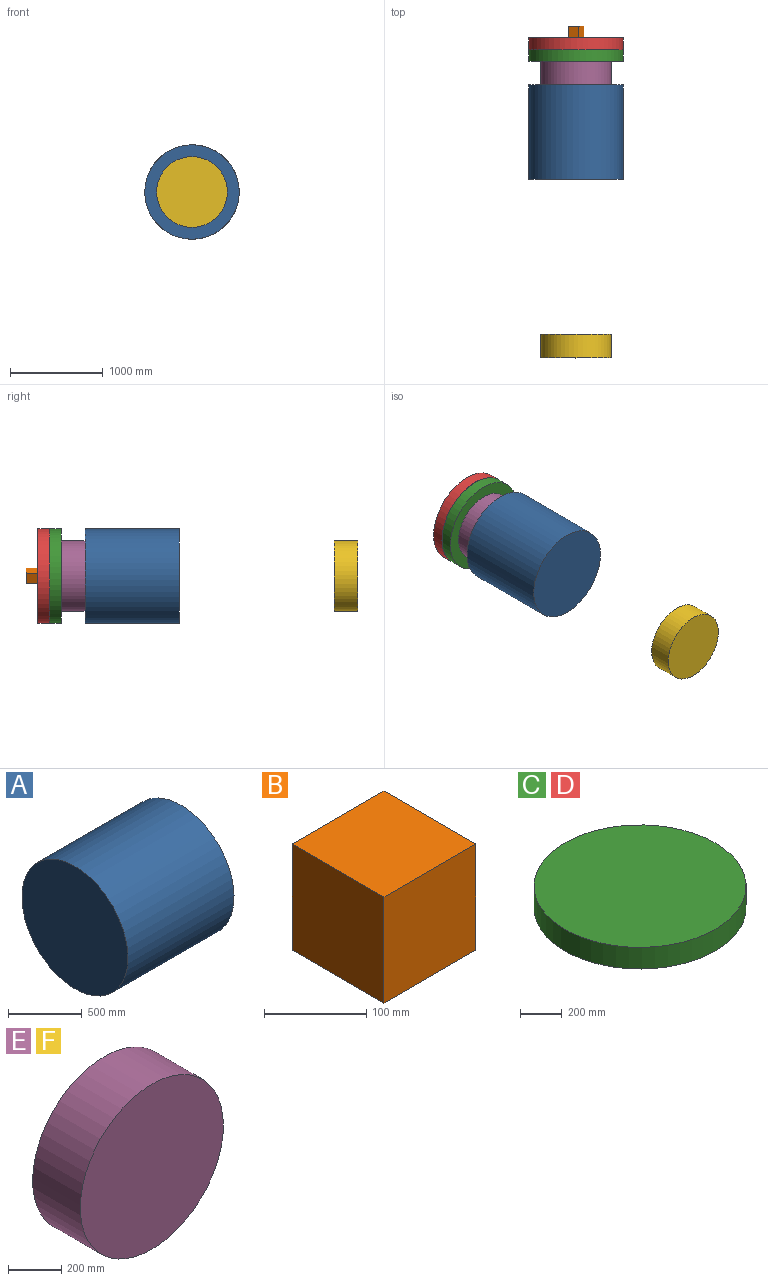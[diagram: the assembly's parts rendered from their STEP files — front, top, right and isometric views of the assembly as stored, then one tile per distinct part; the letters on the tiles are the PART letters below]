
ASSEMBLY  parts=6 mates=5
PART A: 3 faces, bbox 1016x1016x1016 mm
  f0: cylinder r=508mm len=1016mm, axis (-1,0,0), area 3242927.9mm2, adj f1,f2
  f1: plane 1016x1016mm, normal (1,0,0), area 810732mm2, adj f0
  f2: plane 1016x1016mm, normal (-1,0,0), area 810732mm2, adj f0
PART B: 6 faces, bbox 127x127x127 mm
  f0: plane 127x127mm, normal (-1,0,0), area 16129mm2, adj f1,f3,f4,f5
  f1: plane 127x127mm, normal (0,1,0), area 16129mm2, adj f0,f2,f4,f5
  f2: plane 127x127mm, normal (1,0,0), area 16129mm2, adj f1,f3,f4,f5
  f3: plane 127x127mm, normal (0,-1,0), area 16129mm2, adj f0,f2,f4,f5
  f4: plane 127x127mm, normal (0,0,-1), area 16129mm2, adj f0,f1,f2,f3
  f5: plane 127x127mm, normal (0,0,1), area 16129mm2, adj f0,f1,f2,f3
PART C: 3 faces, bbox 1016x1016x127 mm
  f0: cylinder r=508mm len=1016mm, axis (0,0,-1), area 405366mm2, adj f1,f2
  f1: plane 1016x1016mm, normal (0,0,1), area 810732mm2, adj f0
  f2: plane 1016x1016mm, normal (0,0,-1), area 810732mm2, adj f0
PART D: same geometry as C
PART E: 3 faces, bbox 762x254x762 mm
  f0: cylinder r=381mm len=762mm, axis (0,1,0), area 608049mm2, adj f1,f2
  f1: plane 762x762mm, normal (0,-1,0), area 456036.7mm2, adj f0
  f2: plane 762x762mm, normal (0,1,0), area 456036.7mm2, adj f0
PART F: same geometry as E
PLACE A rot(axis=(0.64,-0.64,-0.42),134.1deg) t=(52.41,1931.97,957.85)mm
PLACE B rot(axis=(0,1,0),152.7deg) t=(116.2,2566.97,938.16)mm
PLACE C rot(axis=(0.42,-0.64,0.64),134.1deg) t=(60.04,2312.97,954.16)mm
PLACE D rot(axis=(0.4,-0.65,0.65),136.8deg) t=(60.8,2439.97,956.35)mm
PLACE E rot(axis=(0,-1,0),113deg) t=(60.02,2185.97,944.69)mm
PLACE F t=(0,-752.78,946.68)mm fixed
MATE fastened E.f0 <-> C.f0  axis (0,1,0) through (30.67,2185.97,965.54)mm
MATE cylindrical A.f0 <-> F.f0  axis (0,-1,0) through (30.67,915.97,965.54)mm
MATE fastened D.f0 <-> B.f3  axis (0,1,0) through (30.67,2439.97,965.54)mm
MATE revolute C.f0 <-> D.f0  axis (0,1,0) through (30.67,2312.97,965.54)mm
MATE fastened E.f0 <-> A.f0  axis (0,-1,0) through (30.67,1931.97,965.54)mm
